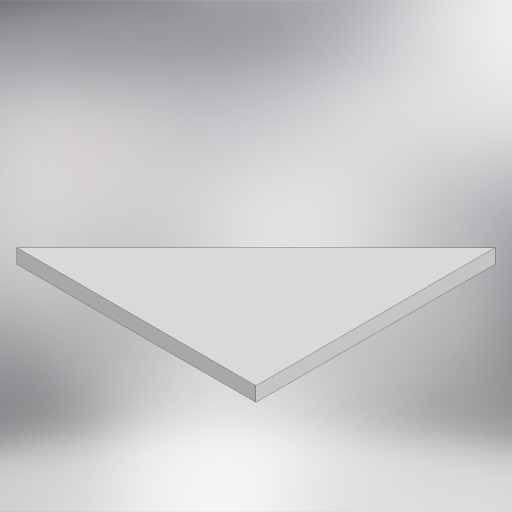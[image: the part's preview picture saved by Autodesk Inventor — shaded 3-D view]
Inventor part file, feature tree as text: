
AUTODESK INVENTOR PART (.ipt)
format: ipt  version: 2023 (Build 270158000, 158)  size: 284,672 bytes
history: native  units: mm
features: other x1, extrude x1, sketch x1
ambient origin geometry x8: Origin, YZ Plane, XZ Plane, XY Plane, X Axis, Y Axis, Z Axis, Center Point
bodies: Body1 (feature_tree)
feature tree (3):
  other  "Sólido1"
  extrude  "Extrusão1"  Depth=3.0mm TaperAngle=0.0deg
  sketch  "Esboço1"  dims[d0=50.0mm d1=3.0mm d2=0.0mm]
